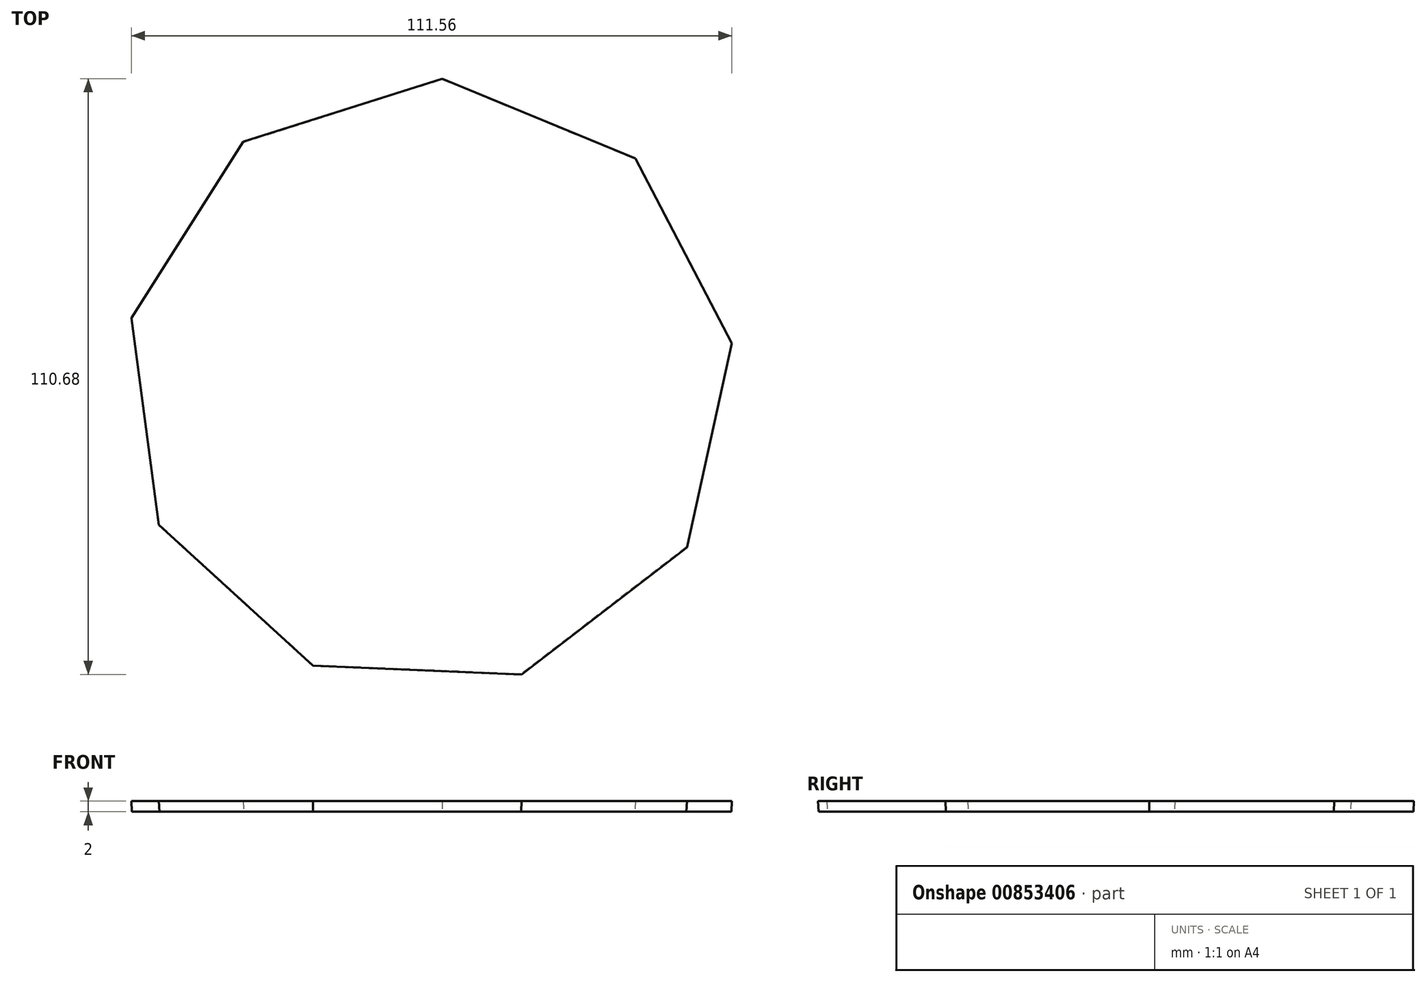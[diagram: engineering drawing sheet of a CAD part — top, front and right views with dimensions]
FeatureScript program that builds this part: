
annotation { "Feature Type Name" : "Feature", "Feature Type Description" : "" }
export const myFeature = defineFeature(function(context is Context, id is Id, definition is map)
    precondition{}
    {
        {
            var Q0;
            Q0=qCreatedBy(makeId("Top.planeOp"),FACE);
            var sketch = newSketch(context, id + "F0", { "sketchPlane" : qUnion([Q0])});
            skCircle(sketch, "E0.cCircle", {"center": v(63.81, 136.94) * mm, "radius": 56.58 * mm, "construction": true});
            skLineSegment(sketch, "E0.0", {"start": v(42.22, 84.65) * mm, "end": v(13.66, 110.76) * mm});
            skLineSegment(sketch, "E0.1", {"start": v(13.66, 110.76) * mm, "end": v(8.56, 149.12) * mm});
            skLineSegment(sketch, "E0.2", {"start": v(8.56, 149.12) * mm, "end": v(29.32, 181.78) * mm});
            skLineSegment(sketch, "E0.3", {"start": v(29.32, 181.78) * mm, "end": v(66.21, 193.47) * mm});
            skLineSegment(sketch, "E0.4", {"start": v(66.21, 193.47) * mm, "end": v(101.98, 178.7) * mm});
            skLineSegment(sketch, "E0.5", {"start": v(101.98, 178.7) * mm, "end": v(119.9, 144.4) * mm});
            skLineSegment(sketch, "E0.6", {"start": v(119.9, 144.4) * mm, "end": v(111.56, 106.6) * mm});
            skLineSegment(sketch, "E0.7", {"start": v(111.56, 106.6) * mm, "end": v(80.89, 83) * mm});
            skLineSegment(sketch, "E0.8", {"start": v(80.89, 83) * mm, "end": v(42.22, 84.65) * mm});
            skSolve(sketch);
        }
        {
            var Q0;
            Q0=makeQuery(id+"F0.imprint","IMPRINT",FACE,{"disambiguationData":[TD([[makeQuery(id+"F0.imprint","IMPRINT",EDGE,{"derivedFrom":sQuery(id+"F0.wireOp",EDGE,"E0.0")}),-1.0]])]});
            extrude(context, id + "F1", {"entities" : qUnion([Q0]), "depth" : 2 * mm, "offsetDistance" : 25.4 * mm, "hasDraft" : true, "draftAngle" : 3 * degree});
        }
    });
